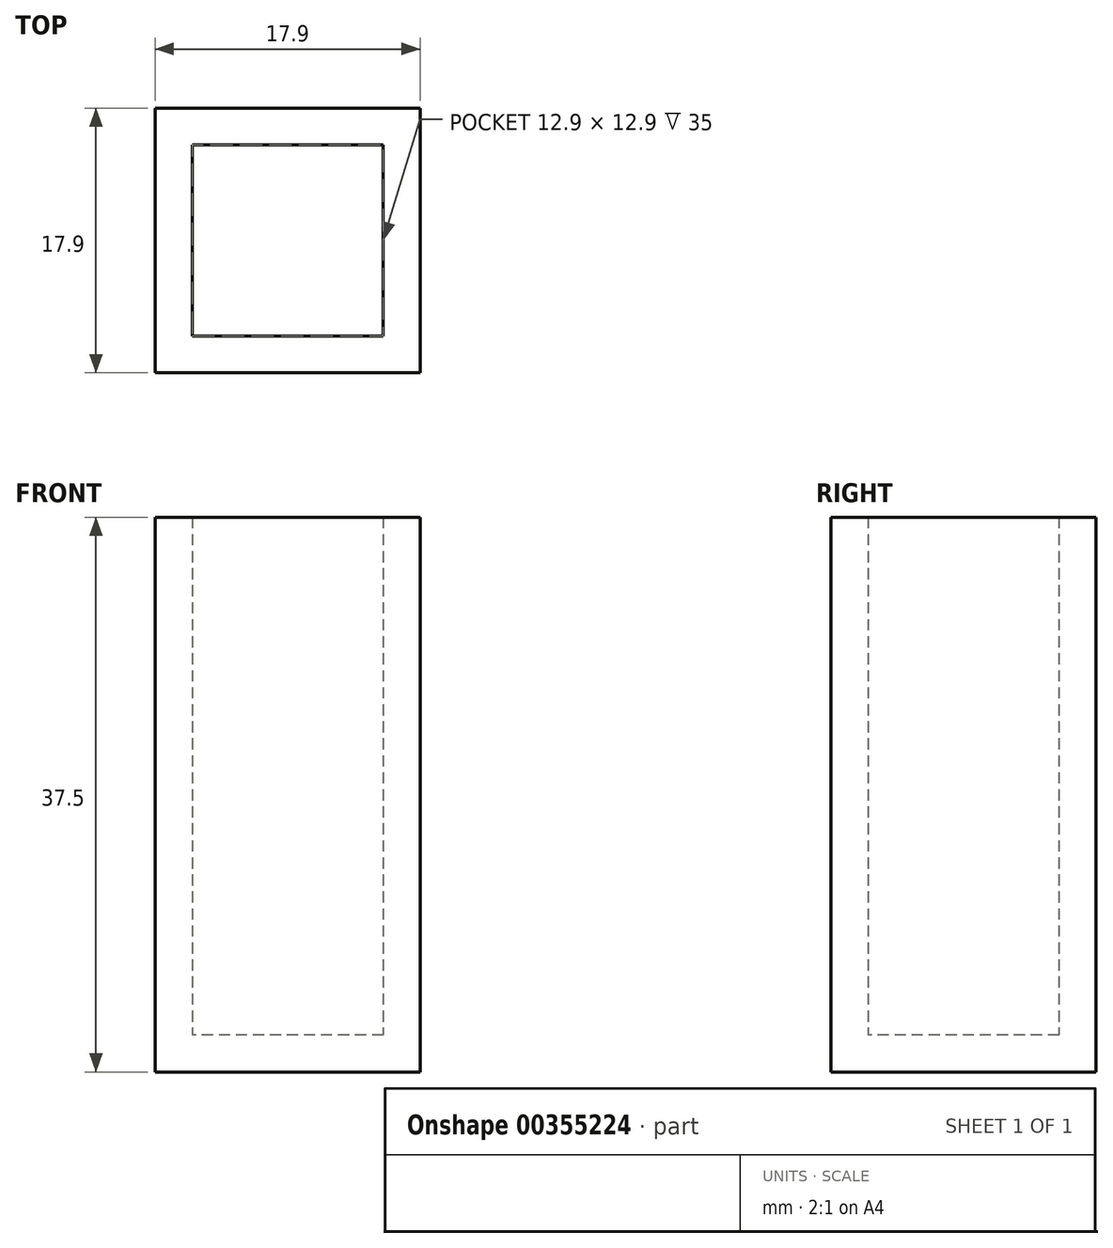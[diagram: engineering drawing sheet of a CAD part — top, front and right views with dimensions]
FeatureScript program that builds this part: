
annotation { "Feature Type Name" : "Feature", "Feature Type Description" : "" }
export const myFeature = defineFeature(function(context is Context, id is Id, definition is map)
    precondition{}
    {
        {
            var Q0;
            Q0=qCreatedBy(makeId("Top.planeOp"),FACE);
            var sketch = newSketch(context, id + "F0", { "sketchPlane" : qUnion([Q0])});
            skLineSegment(sketch, "E0.bottom", {"start": v(6.45, 6.45) * mm, "end": v(-6.45, 6.45) * mm});
            skLineSegment(sketch, "E0.top", {"start": v(6.45, -6.45) * mm, "end": v(-6.45, -6.45) * mm});
            skLineSegment(sketch, "E0.left", {"start": v(6.45, 6.45) * mm, "end": v(6.45, -6.45) * mm});
            skLineSegment(sketch, "E0.right", {"start": v(-6.45, 6.45) * mm, "end": v(-6.45, -6.45) * mm});
            skPoint(sketch, "E0.middle", {"position": v(0, 0) * mm});
            skSolve(sketch);
        }
        {
            var Q0;
            Q0 = qSketchRegion(id + "F0", true);
            extrude(context, id + "F1", {"entities" : qUnion([Q0]), "depth" : 35 * mm});
        }
        {
            var Q0;
            Q0=makeQuery(id+"F1.opExtrude","CAP_FACE",FACE,{"disambiguationData":[OSD([sQuery(id+"F0.wireOp",EDGE,"E0.bottom"),sQuery(id+"F0.wireOp",EDGE,"E0.top"),sQuery(id+"F0.wireOp",EDGE,"E0.left"),sQuery(id+"F0.wireOp",EDGE,"E0.right")])],"isStart":false});
            shell(context, id + "F2", {"entities" : qUnion([Q0]), "thickness" : 2.5 * mm, "oppositeDirection" : true});
        }
    });
